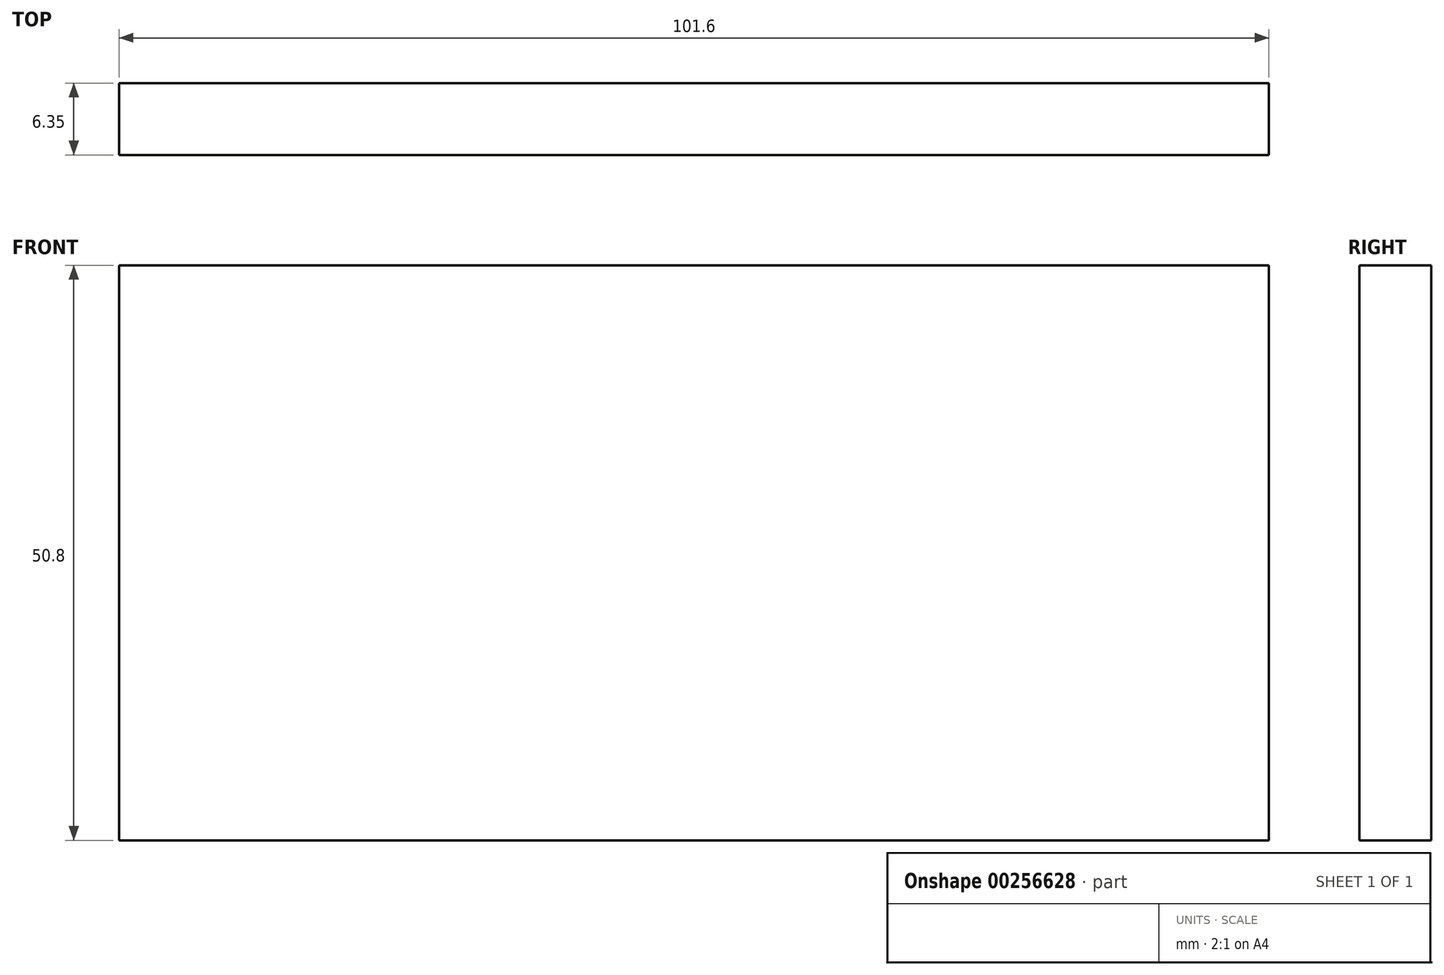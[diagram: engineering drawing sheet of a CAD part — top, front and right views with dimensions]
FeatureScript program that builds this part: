
annotation { "Feature Type Name" : "Feature", "Feature Type Description" : "" }
export const myFeature = defineFeature(function(context is Context, id is Id, definition is map)
    precondition{}
    {
        {
            var Q0;
            Q0=qCreatedBy(makeId("Front.planeOp"),FACE);
            var sketch = newSketch(context, id + "F0", { "sketchPlane" : qUnion([Q0])});
            skLineSegment(sketch, "E0.bottom", {"start": v(-50.8, 25.4) * mm, "end": v(50.8, 25.4) * mm});
            skLineSegment(sketch, "E0.top", {"start": v(-50.8, -25.4) * mm, "end": v(50.8, -25.4) * mm});
            skLineSegment(sketch, "E0.left", {"start": v(-50.8, 25.4) * mm, "end": v(-50.8, -25.4) * mm});
            skLineSegment(sketch, "E0.right", {"start": v(50.8, 25.4) * mm, "end": v(50.8, -25.4) * mm});
            skPoint(sketch, "E0.middle", {"position": v(0, 0) * mm});
            skSolve(sketch);
        }
        {
            var Q0;
            Q0=makeQuery(id+"F0.imprint","IMPRINT",FACE,{"disambiguationData":[TD([[makeQuery(id+"F0.imprint","IMPRINT",EDGE,{"derivedFrom":sQuery(id+"F0.wireOp",EDGE,"E0.bottom")}),-1.0]])]});
            extrude(context, id + "F1", {"entities" : qUnion([Q0]), "depth" : 6.35 * mm});
        }
    });
